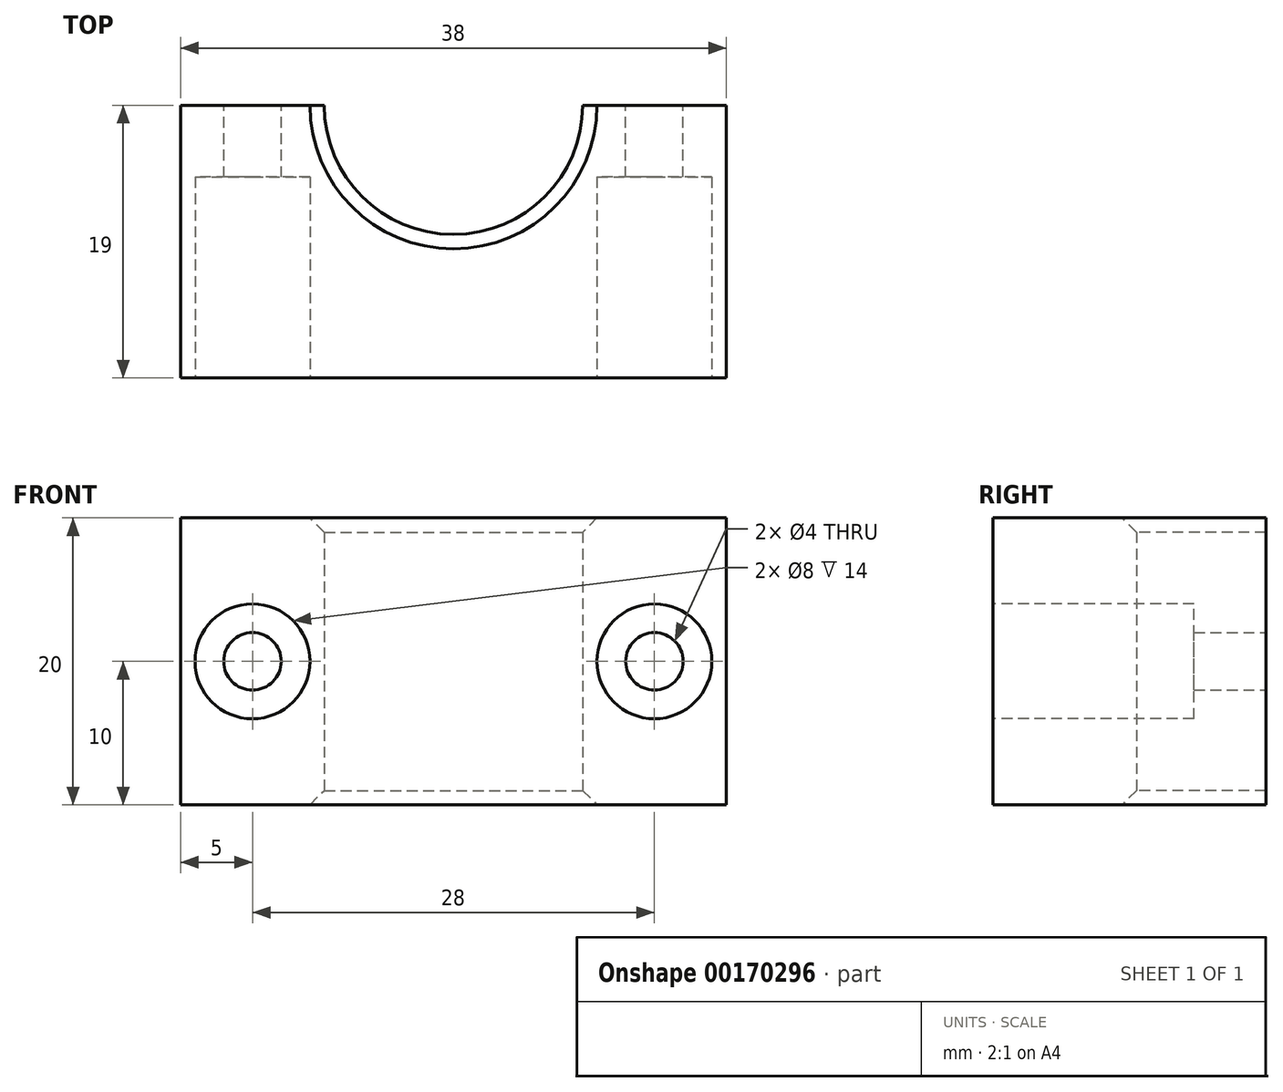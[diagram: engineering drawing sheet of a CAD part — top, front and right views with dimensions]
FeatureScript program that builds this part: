
annotation { "Feature Type Name" : "Feature", "Feature Type Description" : "" }
export const myFeature = defineFeature(function(context is Context, id is Id, definition is map)
    precondition{}
    {
        {
            var Q0;
            Q0=qCreatedBy(makeId("Top.planeOp"),FACE);
            var sketch = newSketch(context, id + "F0", { "sketchPlane" : qUnion([Q0])});
            skLineSegment(sketch, "E0.bottom", {"start": v(-19, 9.5) * mm, "end": v(-9, 9.5) * mm});
            skLineSegment(sketch, "E0.top", {"start": v(-19, -9.5) * mm, "end": v(19, -9.5) * mm});
            skLineSegment(sketch, "E0.left", {"start": v(-19, 9.5) * mm, "end": v(-19, -9.5) * mm});
            skLineSegment(sketch, "E0.right", {"start": v(19, 9.5) * mm, "end": v(19, -9.5) * mm});
            skArc(sketch, "E1", {"start": v(-9, 9.5) * mm, "mid": v(0, 0.5) * mm, "end": v(9, 9.5) * mm});
            skLineSegment(sketch, "E2.trimOffspring", {"start": v(9, 9.5) * mm, "end": v(19, 9.5) * mm});
            skSolve(sketch);
        }
        {
            var Q0;
            Q0=qSketchRegion(id+"F0",true);
            extrude(context, id + "F1", {"entities" : qUnion([Q0]), "depth" : 20 * mm});
        }
        {
            var Q0;
            Q0=makeQuery(id+"F1.opExtrude","SWEPT_FACE",FACE,{"disambiguationData":[OSD([sQuery(id+"F0.wireOp",EDGE,"E0.bottom")])]});
            var sketch = newSketch(context, id + "F2", { "sketchPlane" : qUnion([Q0])});
            skCircle(sketch, "E3", {"center": v(-14, 10) * mm, "radius": 2 * mm});
            skCircle(sketch, "E4", {"center": v(14, 10) * mm, "radius": 2 * mm});
            skSolve(sketch);
        }
        {
            var Q0;
            Q0=qSketchRegion(id+"F2",true);
            extrude(context, id + "F3", {"entities" : qUnion([Q0]), "operationType" : NewBodyOperationType.REMOVE, "endBound" : BoundingType.THROUGH_ALL, "oppositeDirection" : true, "depth" : 25 * mm});
        }
        {
            var Q0;
            Q0=makeQuery(id+"F1.opExtrude","SWEPT_FACE",FACE,{"disambiguationData":[OSD([sQuery(id+"F0.wireOp",EDGE,"E0.top")])]});
            var sketch = newSketch(context, id + "F4", { "sketchPlane" : qUnion([Q0])});
            skCircle(sketch, "E5", {"center": v(-14, 10) * mm, "radius": 4 * mm});
            skCircle(sketch, "E6", {"center": v(14, 10) * mm, "radius": 4 * mm});
            skSolve(sketch);
        }
        {
            var Q0;
            Q0 = qSketchRegion(id + "F4", true);
            extrude(context, id + "F5", {"entities" : qUnion([Q0]), "operationType" : NewBodyOperationType.REMOVE, "oppositeDirection" : true, "depth" : 14 * mm});
        }
        {
            var Q0;
            Q0=makeQuery(id+"F1.opExtrude","CAP_EDGE",EDGE,{"disambiguationData":[OSD([sQuery(id+"F0.wireOp",EDGE,"E1")])],"isStart":true});
            var Q1;
            Q1=makeQuery(id+"F1.opExtrude","CAP_EDGE",EDGE,{"disambiguationData":[OSD([sQuery(id+"F0.wireOp",EDGE,"E1")])],"isStart":false});
            chamfer(context, id + "F6", {"entities" : qUnion([Q0, Q1]), "width" : 1 * mm, "tangentPropagation" : true});
        }
    });
